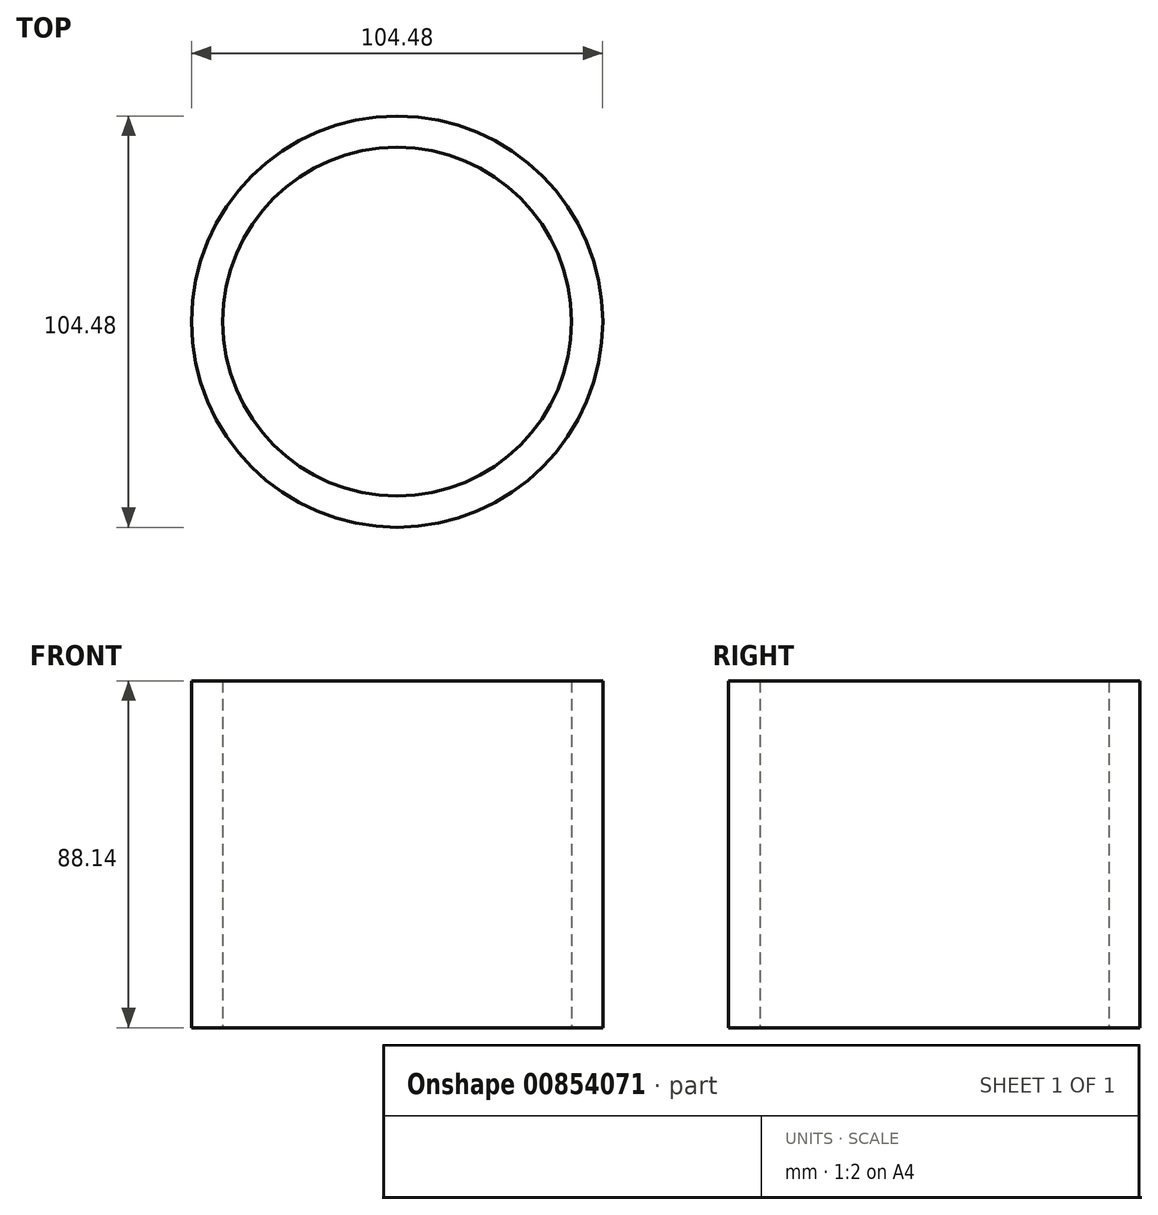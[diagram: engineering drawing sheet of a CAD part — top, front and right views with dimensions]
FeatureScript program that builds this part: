
annotation { "Feature Type Name" : "Feature", "Feature Type Description" : "" }
export const myFeature = defineFeature(function(context is Context, id is Id, definition is map)
    precondition{}
    {
        {
            var Q0;
            Q0=qCreatedBy(makeId("Top.planeOp"),FACE);
            var sketch = newSketch(context, id + "F0", { "sketchPlane" : qUnion([Q0])});
            skCircle(sketch, "E0", {"center": v(0, 0) * mm, "radius": 52.24 * mm});
            skSolve(sketch);
        }
        {
            var Q0;
            Q0=qCreatedBy(makeId("Top.planeOp"),FACE);
            var sketch = newSketch(context, id + "F1", { "sketchPlane" : qUnion([Q0])});
            skCircle(sketch, "E1", {"center": v(0, 0) * mm, "radius": 44.32 * mm});
            skSolve(sketch);
        }
        {
            var Q0;
            Q0=makeQuery(id+"F0.imprint","IMPRINT",FACE,{"disambiguationData":[TD([[makeQuery(id+"F0.imprint","IMPRINT",EDGE,{"derivedFrom":sQuery(id+"F0.wireOp",EDGE,"E0")}),1.0]])]});
            var Q1;
            Q1=makeQuery(id+"F1.imprint","IMPRINT",FACE,{"disambiguationData":[TD([[makeQuery(id+"F1.imprint","IMPRINT",EDGE,{"derivedFrom":sQuery(id+"F1.wireOp",EDGE,"E1")}),1.0]])]});
            extrude(context, id + "F2", {"entities" : qUnion([Q0, Q1]), "depth" : 88.14 * mm, "offsetDistance" : 25.4 * mm});
        }
    });
